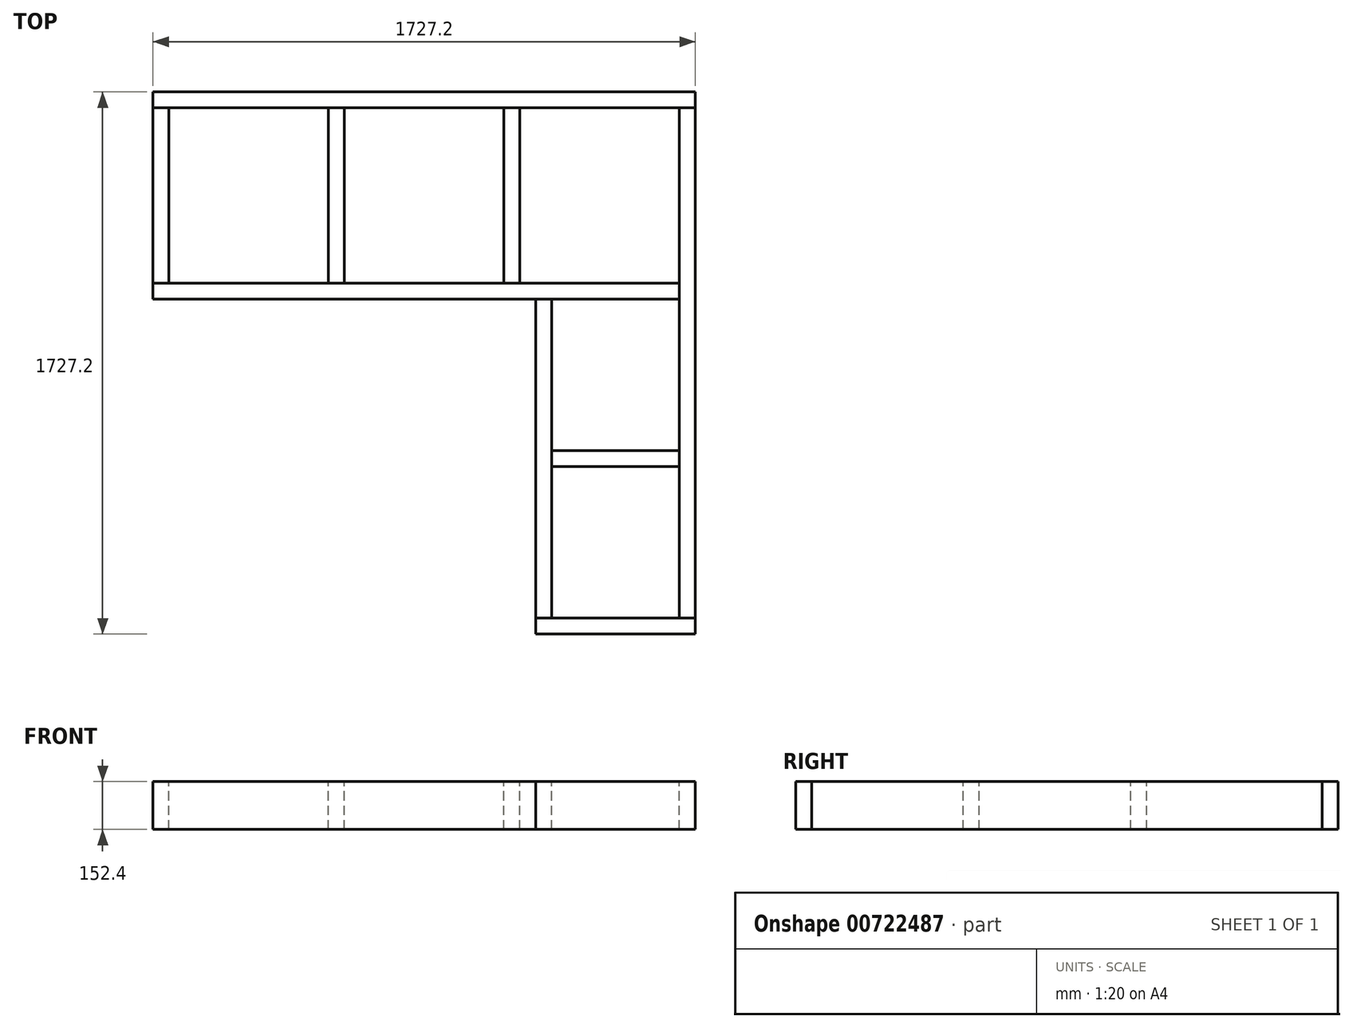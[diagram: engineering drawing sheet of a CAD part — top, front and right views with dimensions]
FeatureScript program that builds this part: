
annotation { "Feature Type Name" : "Feature", "Feature Type Description" : "" }
export const myFeature = defineFeature(function(context is Context, id is Id, definition is map)
    precondition{}
    {
        {
            var Q0;
            Q0=qCreatedBy(makeId("Top.planeOp"),FACE);
            var sketch = newSketch(context, id + "F0", { "sketchPlane" : qUnion([Q0])});
            skLineSegment(sketch, "E0.bottom", {"start": v(0, 0) * mm, "end": v(1727.2, 0) * mm});
            skLineSegment(sketch, "E0.top", {"start": v(0, -50.8) * mm, "end": v(1727.2, -50.8) * mm});
            skLineSegment(sketch, "E0.left", {"start": v(0, 0) * mm, "end": v(0, -50.8) * mm});
            skLineSegment(sketch, "E0.right", {"start": v(1727.2, 0) * mm, "end": v(1727.2, -50.8) * mm});
            skLineSegment(sketch, "E1.bottom", {"start": v(0, -50.8) * mm, "end": v(50.8, -50.8) * mm});
            skLineSegment(sketch, "E1.top", {"start": v(0, -609.6) * mm, "end": v(50.8, -609.6) * mm});
            skLineSegment(sketch, "E1.left", {"start": v(0, -50.8) * mm, "end": v(0, -609.6) * mm});
            skLineSegment(sketch, "E1.right", {"start": v(50.8, -50.8) * mm, "end": v(50.8, -609.6) * mm});
            skLineSegment(sketch, "E2.bottom", {"start": v(1727.2, -50.8) * mm, "end": v(1676.4, -50.8) * mm});
            skLineSegment(sketch, "E2.top", {"start": v(1727.2, -1676.4) * mm, "end": v(1676.4, -1676.4) * mm});
            skLineSegment(sketch, "E2.left", {"start": v(1727.2, -50.8) * mm, "end": v(1727.2, -1676.4) * mm});
            skLineSegment(sketch, "E2.right", {"start": v(1676.4, -50.8) * mm, "end": v(1676.4, -1676.4) * mm});
            skLineSegment(sketch, "E3.bottom", {"start": v(0, -609.6) * mm, "end": v(1676.4, -609.6) * mm});
            skLineSegment(sketch, "E3.top", {"start": v(0, -660.4) * mm, "end": v(1676.4, -660.4) * mm});
            skLineSegment(sketch, "E3.left", {"start": v(0, -609.6) * mm, "end": v(0, -660.4) * mm});
            skLineSegment(sketch, "E3.right", {"start": v(1676.4, -609.6) * mm, "end": v(1676.4, -660.4) * mm});
            skLineSegment(sketch, "E4.bottom", {"start": v(1727.2, -1676.4) * mm, "end": v(1219.2, -1676.4) * mm});
            skLineSegment(sketch, "E4.top", {"start": v(1727.2, -1727.2) * mm, "end": v(1219.2, -1727.2) * mm});
            skLineSegment(sketch, "E4.left", {"start": v(1727.2, -1676.4) * mm, "end": v(1727.2, -1727.2) * mm});
            skLineSegment(sketch, "E4.right", {"start": v(1219.2, -1676.4) * mm, "end": v(1219.2, -1727.2) * mm});
            skLineSegment(sketch, "E5.bottom", {"start": v(1219.2, -1676.4) * mm, "end": v(1270, -1676.4) * mm});
            skLineSegment(sketch, "E5.top", {"start": v(1219.2, -660.4) * mm, "end": v(1270, -660.4) * mm});
            skLineSegment(sketch, "E5.left", {"start": v(1219.2, -1676.4) * mm, "end": v(1219.2, -660.4) * mm});
            skLineSegment(sketch, "E5.right", {"start": v(1270, -1676.4) * mm, "end": v(1270, -660.4) * mm});
            skLineSegment(sketch, "E6", {"start": v(1270, -1676.4) * mm, "end": v(1270, -1193.8) * mm});
            skLineSegment(sketch, "E7.bottom", {"start": v(1270, -1193.8) * mm, "end": v(1676.4, -1193.8) * mm});
            skLineSegment(sketch, "E7.top", {"start": v(1270, -1143) * mm, "end": v(1676.4, -1143) * mm});
            skLineSegment(sketch, "E7.left", {"start": v(1270, -1193.8) * mm, "end": v(1270, -1143) * mm});
            skLineSegment(sketch, "E7.right", {"start": v(1676.4, -1193.8) * mm, "end": v(1676.4, -1143) * mm});
            skLineSegment(sketch, "E8", {"start": v(50.8, -609.6) * mm, "end": v(558.8, -609.6) * mm});
            skLineSegment(sketch, "E9.bottom", {"start": v(558.8, -609.6) * mm, "end": v(609.6, -609.6) * mm});
            skLineSegment(sketch, "E9.top", {"start": v(558.8, -50.8) * mm, "end": v(609.6, -50.8) * mm});
            skLineSegment(sketch, "E9.left", {"start": v(558.8, -609.6) * mm, "end": v(558.8, -50.8) * mm});
            skLineSegment(sketch, "E9.right", {"start": v(609.6, -609.6) * mm, "end": v(609.6, -50.8) * mm});
            skLineSegment(sketch, "E10", {"start": v(609.6, -609.6) * mm, "end": v(1117.6, -609.6) * mm});
            skLineSegment(sketch, "E11.bottom", {"start": v(1117.6, -609.6) * mm, "end": v(1168.4, -609.6) * mm});
            skLineSegment(sketch, "E11.top", {"start": v(1117.6, -50.8) * mm, "end": v(1168.4, -50.8) * mm});
            skLineSegment(sketch, "E11.left", {"start": v(1117.6, -609.6) * mm, "end": v(1117.6, -50.8) * mm});
            skLineSegment(sketch, "E11.right", {"start": v(1168.4, -609.6) * mm, "end": v(1168.4, -50.8) * mm});
            skSolve(sketch);
        }
        {
            var Q0;
            Q0=makeQuery(id+"F0.imprint","IMPRINT",FACE,{"disambiguationData":[TD([[makeQuery(id+"F0.imprint","IMPRINT",EDGE,{"derivedFrom":sQuery(id+"F0.wireOp",EDGE,"E0.bottom")}),-1.0]])]});
            extrude(context, id + "F1", {"entities" : qUnion([Q0]), "oppositeDirection" : true, "depth" : 152.4 * mm, "offsetDistance" : 25.4 * mm});
        }
        {
            var Q0;
            Q0=makeQuery(id+"F0.imprint","IMPRINT",FACE,{"disambiguationData":[TD([[makeQuery(id+"F0.imprint","IMPRINT",EDGE,{"derivedFrom":sQuery(id+"F0.wireOp",EDGE,"E1.top")}),1.0]])]});
            extrude(context, id + "F2", {"entities" : qUnion([Q0]), "oppositeDirection" : true, "depth" : 152.4 * mm, "offsetDistance" : 25.4 * mm});
        }
        {
            var Q0;
            {var subQ12=sQuery(id+"F0.wireOp",EDGE,"E1.top");Q0=makeQuery(id+"F0.imprint","IMPRINT",FACE,{"disambiguationData":[TD([[makeQuery(id+"F0.imprint","IMPRINT",EDGE,{"derivedFrom":subQ12}),-1.0]])]});}
            extrude(context, id + "F3", {"entities" : qUnion([Q0]), "oppositeDirection" : true, "depth" : 152.4 * mm, "offsetDistance" : 25.4 * mm});
        }
        {
            var Q0;
            {var subQ2=sQuery(id+"F0.wireOp",EDGE,"E9.left");Q0=makeQuery(id+"F0.imprint","IMPRINT",FACE,{"disambiguationData":[TD([[makeQuery(id+"F0.imprint","IMPRINT",EDGE,{"derivedFrom":subQ2}),-1.0]])]});}
            extrude(context, id + "F4", {"entities" : qUnion([Q0]), "oppositeDirection" : true, "depth" : 152.4 * mm, "offsetDistance" : 25.4 * mm});
        }
        {
            var Q0;
            {var subQ0=sQuery(id+"F0.wireOp",EDGE,"E11.left");Q0=makeQuery(id+"F0.imprint","IMPRINT",FACE,{"disambiguationData":[TD([[makeQuery(id+"F0.imprint","IMPRINT",EDGE,{"derivedFrom":subQ0}),-1.0]])]});}
            extrude(context, id + "F5", {"entities" : qUnion([Q0]), "oppositeDirection" : true, "depth" : 152.4 * mm, "offsetDistance" : 25.4 * mm});
        }
        {
            var Q0;
            {var subQ0=sQuery(id+"F0.wireOp",EDGE,"E7.bottom");Q0=makeQuery(id+"F0.imprint","IMPRINT",FACE,{"disambiguationData":[TD([[makeQuery(id+"F0.imprint","IMPRINT",EDGE,{"derivedFrom":subQ0}),1.0]])]});}
            extrude(context, id + "F6", {"entities" : qUnion([Q0]), "oppositeDirection" : true, "depth" : 152.4 * mm, "offsetDistance" : 25.4 * mm});
        }
        {
            var Q0;
            {var subQ3=sQuery(id+"F0.wireOp",EDGE,"E2.top");Q0=makeQuery(id+"F0.imprint","IMPRINT",FACE,{"disambiguationData":[TD([[makeQuery(id+"F0.imprint","IMPRINT",EDGE,{"derivedFrom":subQ3}),1.0]])]});}
            extrude(context, id + "F7", {"entities" : qUnion([Q0]), "oppositeDirection" : true, "depth" : 152.4 * mm, "offsetDistance" : 25.4 * mm});
        }
        {
            var Q0;
            {var subQ5=sQuery(id+"F0.wireOp",EDGE,"E2.top");Q0=makeQuery(id+"F0.imprint","IMPRINT",FACE,{"disambiguationData":[TD([[makeQuery(id+"F0.imprint","IMPRINT",EDGE,{"derivedFrom":subQ5}),-1.0]])]});}
            extrude(context, id + "F8", {"entities" : qUnion([Q0]), "oppositeDirection" : true, "depth" : 152.4 * mm, "offsetDistance" : 25.4 * mm});
        }
        {
            var Q0;
            {var subQ0=sQuery(id+"F0.wireOp",EDGE,"E5.left");Q0=makeQuery(id+"F0.imprint","IMPRINT",FACE,{"disambiguationData":[TD([[makeQuery(id+"F0.imprint","IMPRINT",EDGE,{"derivedFrom":subQ0}),-1.0]])]});}
            extrude(context, id + "F9", {"entities" : qUnion([Q0]), "oppositeDirection" : true, "depth" : 152.4 * mm, "offsetDistance" : 25.4 * mm});
        }
    });
